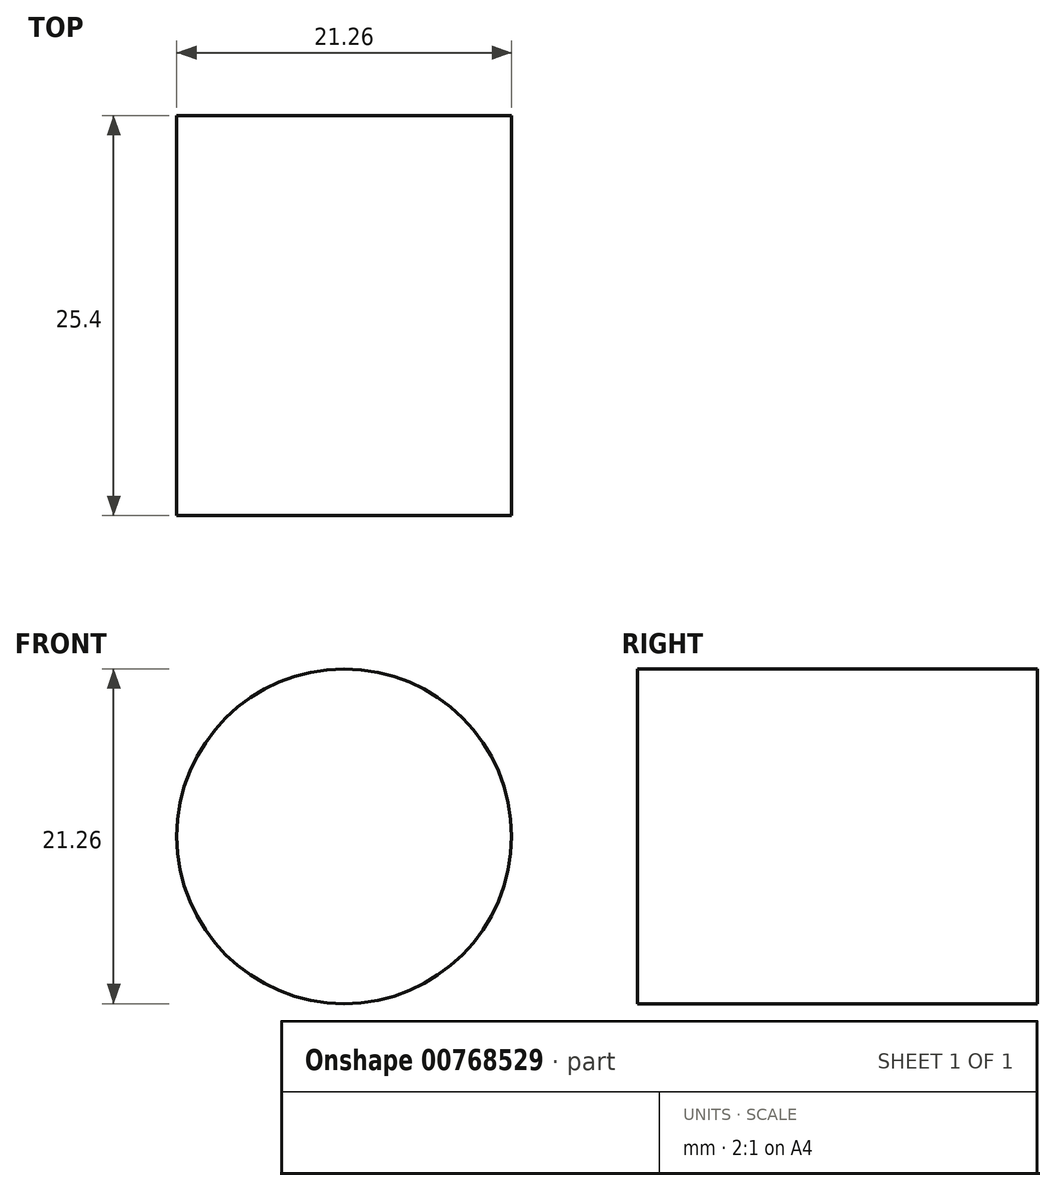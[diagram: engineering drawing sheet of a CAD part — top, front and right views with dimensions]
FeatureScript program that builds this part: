
annotation { "Feature Type Name" : "Feature", "Feature Type Description" : "" }
export const myFeature = defineFeature(function(context is Context, id is Id, definition is map)
    precondition{}
    {
        {
            var Q0;
            Q0=qCreatedBy(makeId("Top.planeOp"),FACE);
            var sketch = newSketch(context, id + "F0", { "sketchPlane" : qUnion([Q0])});
            skCircle(sketch, "E0", {"center": v(0, 0) * mm, "radius": 15.89 * mm});
            skCircle(sketch, "E1", {"center": v(0, 0) * mm, "radius": 13.16 * mm});
            skSolve(sketch);
        }
        {
            var Q0;
            Q0=makeQuery(id+"F0.imprint","IMPRINT",FACE,{"disambiguationData":[TD([[makeQuery(id+"F0.imprint","IMPRINT",EDGE,{"derivedFrom":sQuery(id+"F0.wireOp",EDGE,"E1")}),1.0]])]});
            extrude(context, id + "F1", {"entities" : qUnion([Q0]), "depth" : 4.57 * mm, "offsetDistance" : 25.4 * mm});
        }
        {
            var Q0;
            Q0=qCreatedBy(makeId("Top.planeOp"),FACE);
            var sketch = newSketch(context, id + "F2", { "sketchPlane" : qUnion([Q0])});
            skCircle(sketch, "E2", {"center": v(0, 0) * mm, "radius": 9.86 * mm});
            skSolve(sketch);
        }
        {
            var Q0;
            Q0=makeQuery(id+"F2.imprint","IMPRINT",FACE,{"disambiguationData":[TD([[makeQuery(id+"F2.imprint","IMPRINT",EDGE,{"derivedFrom":sQuery(id+"F2.wireOp",EDGE,"E2")}),1.0]])]});
            extrude(context, id + "F3", {"entities" : qUnion([Q0]), "operationType" : NewBodyOperationType.REMOVE, "oppositeDirection" : true, "depth" : 25.4 * mm, "offsetDistance" : 25.4 * mm});
        }
        {
            var Q0;
            Q0=qCreatedBy(makeId("Top.planeOp"),FACE);
            var sketch = newSketch(context, id + "F4", { "sketchPlane" : qUnion([Q0])});
            skCircle(sketch, "E3", {"center": v(0, 0) * mm, "radius": 8.77 * mm});
            skSolve(sketch);
        }
        {
            var Q0;
            Q0 = qSketchRegion(id + "F4", true);
            var Q1;
            Q1=makeQuery(id+"F1.opExtrude","CAP_FACE",FACE,{"disambiguationData":[OSD([sQuery(id+"F0.wireOp",EDGE,"E1")])],"isStart":false});
            extrude(context, id + "F5", {"entities" : qUnion([Q0, Q1]), "operationType" : NewBodyOperationType.REMOVE, "oppositeDirection" : true, "depth" : 25.4 * mm, "offsetDistance" : 25.4 * mm});
        }
        {
            var Q0;
            Q0=qCreatedBy(makeId("Front.planeOp"),FACE);
            var sketch = newSketch(context, id + "F6", { "sketchPlane" : qUnion([Q0])});
            skCircle(sketch, "E4", {"center": v(0, 0) * mm, "radius": 10.63 * mm});
            skSolve(sketch);
        }
        {
            var Q0;
            Q0 = qSketchRegion(id + "F6", true);
            extrude(context, id + "F7", {"entities" : qUnion([Q0]), "depth" : 25.4 * mm, "offsetDistance" : 25.4 * mm});
        }
    });
